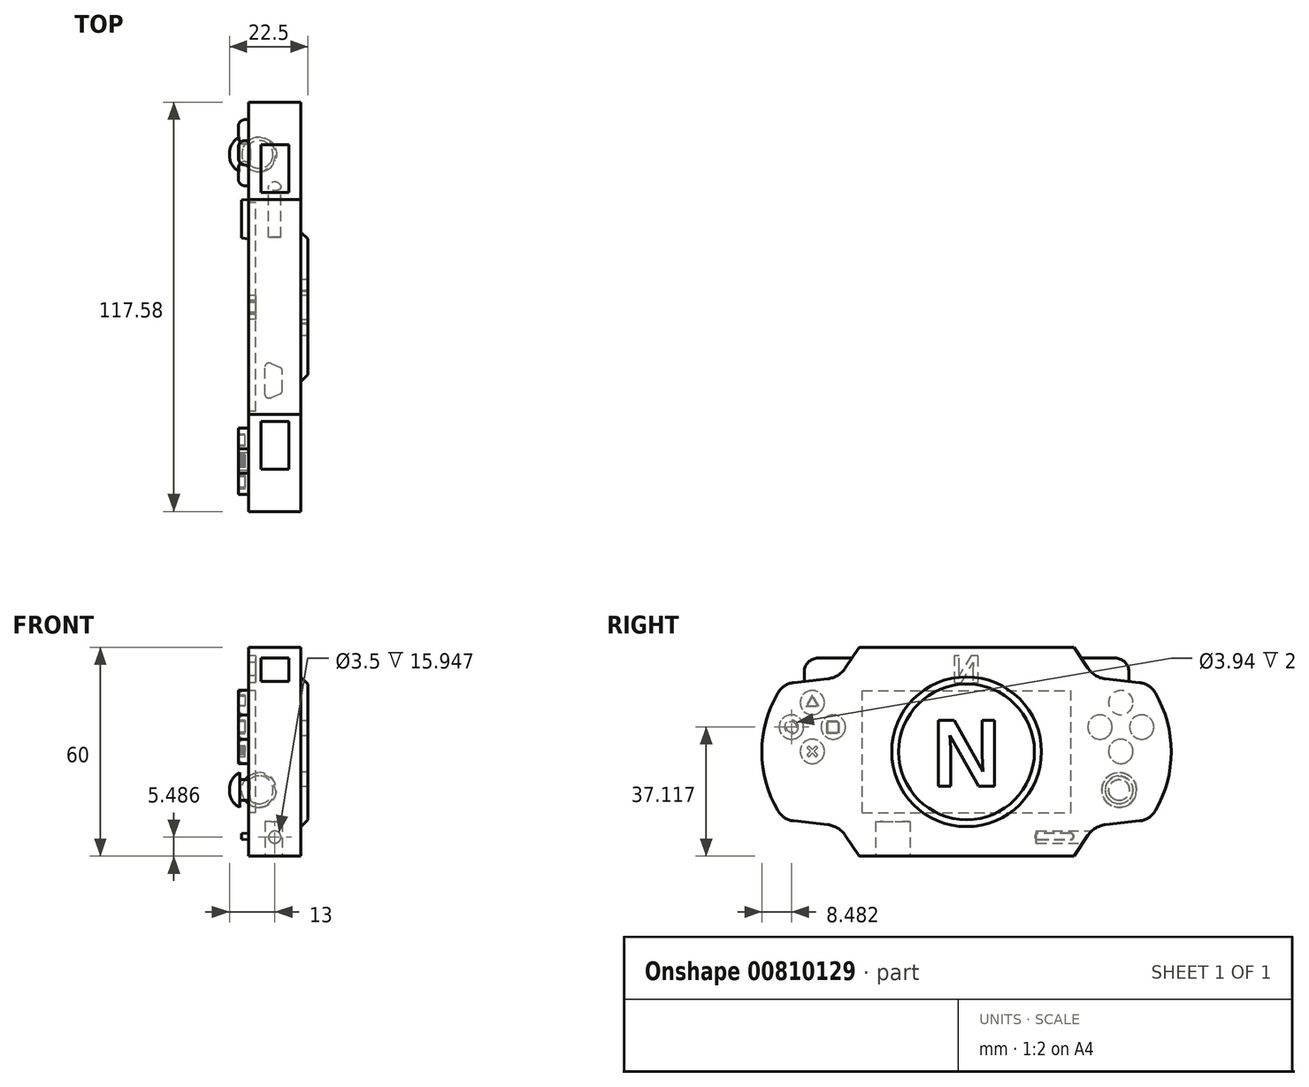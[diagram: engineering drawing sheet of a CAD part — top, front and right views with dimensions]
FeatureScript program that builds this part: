
annotation { "Feature Type Name" : "Feature", "Feature Type Description" : "" }
export const myFeature = defineFeature(function(context is Context, id is Id, definition is map)
    precondition{}
    {
        {
            var Q0;
            Q0=qCreatedBy(makeId("Right.planeOp"),FACE);
            var sketch = newSketch(context, id + "F0", { "sketchPlane" : qUnion([Q0])});
            skLineSegment(sketch, "E0.bottom", {"start": v(-30.9, -30) * mm, "end": v(30.9, -30) * mm});
            skLineSegment(sketch, "E0.top", {"start": v(-30.9, 30) * mm, "end": v(30.9, 30) * mm});
            skLineSegment(sketch, "E0.left", {"start": v(-52.5, -19.53) * mm, "end": v(-52.5, 19.53) * mm});
            skLineSegment(sketch, "E0.right", {"start": v(52.5, -19.53) * mm, "end": v(52.5, 19.53) * mm});
            skPoint(sketch, "E0.middle", {"position": v(0, 0) * mm});
            skLineSegment(sketch, "E1", {"start": v(49.7, 19.85) * mm, "end": v(46.21, 20.24) * mm});
            skLineSegment(sketch, "E2", {"start": v(34.87, 24.03) * mm, "end": v(30.9, 30) * mm});
            skPoint(sketch, "E3.visualSharp", {"position": v(36.68, 21.3) * mm});
            skArc(sketch, "E3.filletArc", {"start": v(34.87, 24.03) * mm, "mid": v(37.06, 21.92) * mm, "end": v(39.92, 20.94) * mm});
            skLineSegment(sketch, "E4", {"start": v(0, 39.51) * mm, "end": v(0, -39.4) * mm});
            skLineSegment(sketch, "E5.MirrorCS", {"start": v(-34.87, 24.03) * mm, "end": v(-30.9, 30) * mm});
            skPoint(sketch, "E6.MirrorP", {"position": v(-36.68, 21.3) * mm});
            skLineSegment(sketch, "E7.MirrorCS", {"start": v(-49.7, 19.85) * mm, "end": v(-46.21, 20.24) * mm});
            skArc(sketch, "E8.MirrorCS", {"start": v(-34.87, 24.03) * mm, "mid": v(-37.06, 21.92) * mm, "end": v(-39.92, 20.94) * mm});
            skLineSegment(sketch, "E9", {"start": v(46.21, 20.24) * mm, "end": v(39.92, 20.94) * mm});
            skLineSegment(sketch, "E10", {"start": v(59.6, 0) * mm, "end": v(-64.27, 0) * mm});
            skLineSegment(sketch, "E11.MirrorCS", {"start": v(49.7, -19.85) * mm, "end": v(46.21, -20.24) * mm});
            skLineSegment(sketch, "E12.MirrorCS", {"start": v(46.21, -20.24) * mm, "end": v(39.92, -20.94) * mm});
            skPoint(sketch, "E13.MirrorP", {"position": v(36.68, -21.3) * mm});
            skLineSegment(sketch, "E14.MirrorCS", {"start": v(34.87, -24.03) * mm, "end": v(30.9, -30) * mm});
            skArc(sketch, "E15.MirrorCS", {"start": v(34.87, -24.03) * mm, "mid": v(37.06, -21.92) * mm, "end": v(39.92, -20.94) * mm});
            skLineSegment(sketch, "E16.MirrorCS", {"start": v(-34.87, -24.03) * mm, "end": v(-30.9, -30) * mm});
            skArc(sketch, "E17.MirrorCS", {"start": v(-34.87, -24.03) * mm, "mid": v(-37.06, -21.92) * mm, "end": v(-39.92, -20.94) * mm});
            skLineSegment(sketch, "E18.MirrorCS", {"start": v(-49.7, -19.85) * mm, "end": v(-46.21, -20.24) * mm});
            skLineSegment(sketch, "E19", {"start": v(-46.21, 20.24) * mm, "end": v(-39.92, 20.94) * mm});
            skLineSegment(sketch, "E20", {"start": v(-46.21, -20.24) * mm, "end": v(-39.92, -20.94) * mm});
            skArc(sketch, "E21", {"start": v(54.2, -16.92) * mm, "mid": v(58.79, 0) * mm, "end": v(54.2, 16.92) * mm});
            skArc(sketch, "E22.MirrorCS", {"start": v(-54.2, -16.92) * mm, "mid": v(-58.79, 0) * mm, "end": v(-54.2, 16.92) * mm});
            skPoint(sketch, "E23.visualSharp", {"position": v(52.5, 19.53) * mm});
            skArc(sketch, "E23.filletArc", {"start": v(54.2, 16.92) * mm, "mid": v(52.3, 18.92) * mm, "end": v(49.7, 19.85) * mm});
            skPoint(sketch, "E24.visualSharp", {"position": v(52.5, -19.53) * mm});
            skArc(sketch, "E24.filletArc", {"start": v(49.7, -19.85) * mm, "mid": v(52.3, -18.92) * mm, "end": v(54.2, -16.92) * mm});
            skPoint(sketch, "E25.visualSharp", {"position": v(-52.5, 19.53) * mm});
            skArc(sketch, "E25.filletArc", {"start": v(-49.7, 19.85) * mm, "mid": v(-52.3, 18.92) * mm, "end": v(-54.2, 16.92) * mm});
            skPoint(sketch, "E26.visualSharp", {"position": v(-52.5, -19.53) * mm});
            skArc(sketch, "E26.filletArc", {"start": v(-54.2, -16.92) * mm, "mid": v(-52.3, -18.92) * mm, "end": v(-49.7, -19.85) * mm});
            skPoint(sketch, "E27.orphan", {"position": v(52.5, 30) * mm});
            skPoint(sketch, "E28.orphan", {"position": v(52.5, -30) * mm});
            skPoint(sketch, "E29.orphan", {"position": v(-52.5, -30) * mm});
            skPoint(sketch, "E30.orphan", {"position": v(-52.5, 30) * mm});
            skSolve(sketch);
        }
        {
            var Q0;
            Q0=qSketchRegion(id+"F0",true);
            extrude(context, id + "F1", {"entities" : qUnion([Q0]), "endBound" : BoundingType.SYMMETRIC, "depth" : 15 * mm, "offsetDistance" : 25 * mm});
        }
        {
            var Q0;
            Q0=qCreatedBy(makeId("Right.planeOp"),FACE);
            var sketch = newSketch(context, id + "F2", { "sketchPlane" : qUnion([Q0])});
            skLineSegment(sketch, "E31.bottom", {"start": v(29.71, 18.85) * mm, "end": v(46.63, 18.85) * mm});
            skLineSegment(sketch, "E31.top", {"start": v(29.71, 26.92) * mm, "end": v(42.63, 26.92) * mm});
            skLineSegment(sketch, "E31.left", {"start": v(29.71, 18.85) * mm, "end": v(29.71, 26.92) * mm});
            skLineSegment(sketch, "E31.right", {"start": v(46.63, 18.85) * mm, "end": v(46.63, 22.92) * mm});
            skPoint(sketch, "E31.middle", {"position": v(38.17, 22.88) * mm});
            skLineSegment(sketch, "E32", {"start": v(0, 47.3) * mm, "end": v(0, -44.62) * mm});
            skLineSegment(sketch, "E33.MirrorCS", {"start": v(-29.71, 26.92) * mm, "end": v(-42.63, 26.92) * mm});
            skLineSegment(sketch, "E34.MirrorCS", {"start": v(-46.63, 18.85) * mm, "end": v(-46.63, 22.92) * mm});
            skLineSegment(sketch, "E35.MirrorCS", {"start": v(-29.71, 18.85) * mm, "end": v(-29.71, 26.92) * mm});
            skLineSegment(sketch, "E36.MirrorCS", {"start": v(-29.71, 18.85) * mm, "end": v(-46.63, 18.85) * mm});
            skPoint(sketch, "E37.visualSharp", {"position": v(46.63, 26.92) * mm});
            skArc(sketch, "E37.filletArc", {"start": v(46.63, 22.92) * mm, "mid": v(45.46, 25.75) * mm, "end": v(42.63, 26.92) * mm});
            skPoint(sketch, "E38.visualSharp", {"position": v(-46.63, 26.92) * mm});
            skArc(sketch, "E38.filletArc", {"start": v(-42.63, 26.92) * mm, "mid": v(-45.46, 25.75) * mm, "end": v(-46.63, 22.92) * mm});
            skSolve(sketch);
        }
        {
            var Q0;
            Q0=makeQuery(id+"F2.imprint","IMPRINT",FACE,{"disambiguationData":[TD([[makeQuery(id+"F2.imprint","IMPRINT",EDGE,{"derivedFrom":sQuery(id+"F2.wireOp",EDGE,"E31.bottom")}),1.0]])]});
            var Q1;
            Q1=makeQuery(id+"F2.imprint","IMPRINT",FACE,{"disambiguationData":[TD([[makeQuery(id+"F2.imprint","IMPRINT",EDGE,{"derivedFrom":sQuery(id+"F2.wireOp",EDGE,"E33.MirrorCS")}),1.0]])]});
            var Q2;
            Q2=qConstructionFilter(qBodyType(qCreatedBy(id+"F2",EDGE),BodyType.WIRE),ConstructionObject.NO);
            extrude(context, id + "F3", {"entities" : qUnion([Q0, Q1]), "operationType" : NewBodyOperationType.ADD, "surfaceEntities" : qUnion([Q2]), "endBound" : BoundingType.SYMMETRIC, "depth" : 8 * mm, "offsetDistance" : 25 * mm});
        }
        {
            var Q0;
            Q0=makeQuery(id+"F1.opExtrude","CAP_FACE",FACE,{"disambiguationData":[OSD([sQuery(id+"F0.wireOp",EDGE,"E0.bottom"),sQuery(id+"F0.wireOp",EDGE,"E0.top"),sQuery(id+"F0.wireOp",EDGE,"E1"),sQuery(id+"F0.wireOp",EDGE,"E2"),sQuery(id+"F0.wireOp",EDGE,"E3.filletArc"),sQuery(id+"F0.wireOp",EDGE,"E5.MirrorCS"),sQuery(id+"F0.wireOp",EDGE,"E7.MirrorCS"),sQuery(id+"F0.wireOp",EDGE,"E8.MirrorCS"),sQuery(id+"F0.wireOp",EDGE,"E9"),sQuery(id+"F0.wireOp",EDGE,"E11.MirrorCS"),sQuery(id+"F0.wireOp",EDGE,"E12.MirrorCS"),sQuery(id+"F0.wireOp",EDGE,"E14.MirrorCS"),sQuery(id+"F0.wireOp",EDGE,"E15.MirrorCS"),sQuery(id+"F0.wireOp",EDGE,"E16.MirrorCS"),sQuery(id+"F0.wireOp",EDGE,"E17.MirrorCS"),sQuery(id+"F0.wireOp",EDGE,"E18.MirrorCS"),sQuery(id+"F0.wireOp",EDGE,"E19"),sQuery(id+"F0.wireOp",EDGE,"E20"),sQuery(id+"F0.wireOp",EDGE,"E21"),sQuery(id+"F0.wireOp",EDGE,"E22.MirrorCS"),sQuery(id+"F0.wireOp",EDGE,"E23.filletArc"),sQuery(id+"F0.wireOp",EDGE,"E24.filletArc"),sQuery(id+"F0.wireOp",EDGE,"E25.filletArc"),sQuery(id+"F0.wireOp",EDGE,"E26.filletArc")])],"isStart":true});
            var sketch = newSketch(context, id + "F4", { "sketchPlane" : qUnion([Q0])});
            skLineSegment(sketch, "E39.bottom", {"start": v(30, -17.5) * mm, "end": v(-30, -17.5) * mm});
            skLineSegment(sketch, "E39.top", {"start": v(30, 17.5) * mm, "end": v(-30, 17.5) * mm});
            skLineSegment(sketch, "E39.left", {"start": v(30, -17.5) * mm, "end": v(30, 17.5) * mm});
            skLineSegment(sketch, "E39.right", {"start": v(-30, -17.5) * mm, "end": v(-30, 17.5) * mm});
            skPoint(sketch, "E39.middle", {"position": v(0, 0) * mm});
            skSolve(sketch);
        }
        {
            var Q0;
            Q0=makeQuery(id+"F4.imprint","IMPRINT",FACE,{"disambiguationData":[TD([[makeQuery(id+"F4.imprint","IMPRINT",EDGE,{"derivedFrom":sQuery(id+"F4.wireOp",EDGE,"E39.bottom")}),-1.0]])]});
            extrude(context, id + "F5", {"entities" : qUnion([Q0]), "operationType" : NewBodyOperationType.REMOVE, "oppositeDirection" : true, "depth" : 2 * mm, "offsetDistance" : 25 * mm});
        }
        {
            var Q0;
            Q0=makeQuery(id+"F1.opExtrude","CAP_FACE",FACE,{"disambiguationData":[OSD([sQuery(id+"F0.wireOp",EDGE,"E0.bottom"),sQuery(id+"F0.wireOp",EDGE,"E0.top"),sQuery(id+"F0.wireOp",EDGE,"E1"),sQuery(id+"F0.wireOp",EDGE,"E2"),sQuery(id+"F0.wireOp",EDGE,"E3.filletArc"),sQuery(id+"F0.wireOp",EDGE,"E5.MirrorCS"),sQuery(id+"F0.wireOp",EDGE,"E7.MirrorCS"),sQuery(id+"F0.wireOp",EDGE,"E8.MirrorCS"),sQuery(id+"F0.wireOp",EDGE,"E9"),sQuery(id+"F0.wireOp",EDGE,"E11.MirrorCS"),sQuery(id+"F0.wireOp",EDGE,"E12.MirrorCS"),sQuery(id+"F0.wireOp",EDGE,"E14.MirrorCS"),sQuery(id+"F0.wireOp",EDGE,"E15.MirrorCS"),sQuery(id+"F0.wireOp",EDGE,"E16.MirrorCS"),sQuery(id+"F0.wireOp",EDGE,"E17.MirrorCS"),sQuery(id+"F0.wireOp",EDGE,"E18.MirrorCS"),sQuery(id+"F0.wireOp",EDGE,"E19"),sQuery(id+"F0.wireOp",EDGE,"E20"),sQuery(id+"F0.wireOp",EDGE,"E21"),sQuery(id+"F0.wireOp",EDGE,"E22.MirrorCS"),sQuery(id+"F0.wireOp",EDGE,"E23.filletArc"),sQuery(id+"F0.wireOp",EDGE,"E24.filletArc"),sQuery(id+"F0.wireOp",EDGE,"E25.filletArc"),sQuery(id+"F0.wireOp",EDGE,"E26.filletArc")])],"isStart":true});
            var sketch = newSketch(context, id + "F6", { "sketchPlane" : qUnion([Q0])});
            skLineSegment(sketch, "E40", {"start": v(-50.3, 7.12) * mm, "end": v(-44.3, 7.12) * mm});
            skLineSegment(sketch, "E41", {"start": v(-44.3, 7.12) * mm, "end": v(-38.3, 7.12) * mm});
            skLineSegment(sketch, "E42", {"start": v(-44.3, 7.12) * mm, "end": v(-44.3, 0.12) * mm});
            skLineSegment(sketch, "E43", {"start": v(-44.3, 7.12) * mm, "end": v(-44.3, 14.12) * mm});
            skCircle(sketch, "E44", {"center": v(-44.3, 14.12) * mm, "radius": 3.5 * mm});
            skCircle(sketch, "E45", {"center": v(-50.3, 7.12) * mm, "radius": 3.5 * mm});
            skCircle(sketch, "E46", {"center": v(-38.3, 7.12) * mm, "radius": 3.5 * mm});
            skCircle(sketch, "E47", {"center": v(-44.3, 0.12) * mm, "radius": 3.5 * mm});
            skLineSegment(sketch, "E48", {"start": v(0, 48.36) * mm, "end": v(0, -44.18) * mm});
            skPoint(sketch, "E48.endSnap0", {"position": v(0, -30) * mm});
            skCircle(sketch, "E49.MirrorC", {"center": v(44.3, 14.12) * mm, "radius": 3.5 * mm});
            skCircle(sketch, "E50.MirrorC", {"center": v(38.3, 7.12) * mm, "radius": 3.5 * mm});
            skCircle(sketch, "E51.MirrorC", {"center": v(44.3, 0.12) * mm, "radius": 3.5 * mm});
            skCircle(sketch, "E52.MirrorC", {"center": v(50.3, 7.12) * mm, "radius": 3.5 * mm});
            skSolve(sketch);
        }
        {
            var Q0;
            Q0 = qSketchRegion(id + "F6", true);
            extrude(context, id + "F7", {"entities" : qUnion([Q0]), "operationType" : NewBodyOperationType.ADD, "depth" : 3 * mm, "offsetDistance" : 25 * mm});
        }
        {
            var Q0;
            Q0=makeQuery(id+"F7.opExtrude","CAP_FACE",FACE,{"disambiguationData":[OSD([sQuery(id+"F6.wireOp",EDGE,"E44")])],"isStart":false});
            var Q1;
            Q1=makeQuery(id+"F7.opExtrude","CAP_FACE",FACE,{"disambiguationData":[OSD([sQuery(id+"F6.wireOp",EDGE,"E46")])],"isStart":false});
            var Q2;
            Q2=makeQuery(id+"F7.opExtrude","CAP_FACE",FACE,{"disambiguationData":[OSD([sQuery(id+"F6.wireOp",EDGE,"E47")])],"isStart":false});
            var Q3;
            Q3=makeQuery(id+"F7.opExtrude","CAP_FACE",FACE,{"disambiguationData":[OSD([sQuery(id+"F6.wireOp",EDGE,"E45")])],"isStart":false});
            fillet(context, id + "F8", {"entities" : qUnion([Q0, Q1, Q2, Q3]), "radius" : 2 * mm, "tangentPropagation" : true, "allowEdgeOverflow" : false});
        }
        {
            var Q0;
            Q0=makeQuery(id+"F1.opExtrude","CAP_FACE",FACE,{"disambiguationData":[OSD([sQuery(id+"F0.wireOp",EDGE,"E0.bottom"),sQuery(id+"F0.wireOp",EDGE,"E0.top"),sQuery(id+"F0.wireOp",EDGE,"E1"),sQuery(id+"F0.wireOp",EDGE,"E2"),sQuery(id+"F0.wireOp",EDGE,"E3.filletArc"),sQuery(id+"F0.wireOp",EDGE,"E5.MirrorCS"),sQuery(id+"F0.wireOp",EDGE,"E7.MirrorCS"),sQuery(id+"F0.wireOp",EDGE,"E8.MirrorCS"),sQuery(id+"F0.wireOp",EDGE,"E9"),sQuery(id+"F0.wireOp",EDGE,"E11.MirrorCS"),sQuery(id+"F0.wireOp",EDGE,"E12.MirrorCS"),sQuery(id+"F0.wireOp",EDGE,"E14.MirrorCS"),sQuery(id+"F0.wireOp",EDGE,"E15.MirrorCS"),sQuery(id+"F0.wireOp",EDGE,"E16.MirrorCS"),sQuery(id+"F0.wireOp",EDGE,"E17.MirrorCS"),sQuery(id+"F0.wireOp",EDGE,"E18.MirrorCS"),sQuery(id+"F0.wireOp",EDGE,"E19"),sQuery(id+"F0.wireOp",EDGE,"E20"),sQuery(id+"F0.wireOp",EDGE,"E21"),sQuery(id+"F0.wireOp",EDGE,"E22.MirrorCS"),sQuery(id+"F0.wireOp",EDGE,"E23.filletArc"),sQuery(id+"F0.wireOp",EDGE,"E24.filletArc"),sQuery(id+"F0.wireOp",EDGE,"E25.filletArc"),sQuery(id+"F0.wireOp",EDGE,"E26.filletArc")])],"isStart":false});
            var sketch = newSketch(context, id + "F9", { "sketchPlane" : qUnion([Q0])});
            skCircle(sketch, "E53", {"center": v(0, 0) * mm, "radius": 22.5 * mm});
            skSolve(sketch);
        }
        {
            var Q0;
            Q0 = qSketchRegion(id + "F9", true);
            extrude(context, id + "F10", {"entities" : qUnion([Q0]), "operationType" : NewBodyOperationType.ADD, "depth" : 2 * mm, "offsetDistance" : 25 * mm});
        }
        {
            var Q0;
            Q0=makeQuery(id+"F10.opExtrude","CAP_EDGE",EDGE,{"disambiguationData":[OSD([sQuery(id+"F9.wireOp",EDGE,"E53")])],"isStart":false});
            chamfer(context, id + "F11", {"entities" : qUnion([Q0]), "width" : 3 * mm, "tangentPropagation" : true});
        }
        {
            var Q0;
            Q0=makeQuery(id+"F10.opExtrude","CAP_FACE",FACE,{"disambiguationData":[OSD([sQuery(id+"F9.wireOp",EDGE,"E53")])],"isStart":false});
            var sketch = newSketch(context, id + "F12", { "sketchPlane" : qUnion([Q0])});
            skText(sketch, "E54", { "text": "N\n", "fontName": "Arimo-Bold.ttf"});
            skPoint(sketch, "E55", {"position": v(0, 0) * mm});
            const initialGuessF12  = {"E54": [-0.00995, -0.00989, 1, 0, 0.01978]};
            skSetInitialGuess(sketch, initialGuessF12);
            skSolve(sketch);
        }
        {
            var Q0;
            Q0 = qSketchRegion(id + "F12", true);
            extrude(context, id + "F13", {"entities" : qUnion([Q0]), "operationType" : NewBodyOperationType.REMOVE, "oppositeDirection" : true, "depth" : 2 * mm, "offsetDistance" : 25 * mm});
        }
        {
            var Q0;
            Q0=makeQuery(id+"F1.opExtrude","CAP_FACE",FACE,{"disambiguationData":[OSD([sQuery(id+"F0.wireOp",EDGE,"E0.bottom"),sQuery(id+"F0.wireOp",EDGE,"E0.top"),sQuery(id+"F0.wireOp",EDGE,"E1"),sQuery(id+"F0.wireOp",EDGE,"E2"),sQuery(id+"F0.wireOp",EDGE,"E3.filletArc"),sQuery(id+"F0.wireOp",EDGE,"E5.MirrorCS"),sQuery(id+"F0.wireOp",EDGE,"E7.MirrorCS"),sQuery(id+"F0.wireOp",EDGE,"E8.MirrorCS"),sQuery(id+"F0.wireOp",EDGE,"E9"),sQuery(id+"F0.wireOp",EDGE,"E11.MirrorCS"),sQuery(id+"F0.wireOp",EDGE,"E12.MirrorCS"),sQuery(id+"F0.wireOp",EDGE,"E14.MirrorCS"),sQuery(id+"F0.wireOp",EDGE,"E15.MirrorCS"),sQuery(id+"F0.wireOp",EDGE,"E16.MirrorCS"),sQuery(id+"F0.wireOp",EDGE,"E17.MirrorCS"),sQuery(id+"F0.wireOp",EDGE,"E18.MirrorCS"),sQuery(id+"F0.wireOp",EDGE,"E19"),sQuery(id+"F0.wireOp",EDGE,"E20"),sQuery(id+"F0.wireOp",EDGE,"E21"),sQuery(id+"F0.wireOp",EDGE,"E22.MirrorCS"),sQuery(id+"F0.wireOp",EDGE,"E23.filletArc"),sQuery(id+"F0.wireOp",EDGE,"E24.filletArc"),sQuery(id+"F0.wireOp",EDGE,"E25.filletArc"),sQuery(id+"F0.wireOp",EDGE,"E26.filletArc")])],"isStart":true});
            var sketch = newSketch(context, id + "F14", { "sketchPlane" : qUnion([Q0])});
            skLineSegment(sketch, "E56.bottom", {"start": v(-20.58, -25.31) * mm, "end": v(-29.84, -25.31) * mm});
            skLineSegment(sketch, "E56.top", {"start": v(-20.58, -23.31) * mm, "end": v(-29.84, -23.31) * mm});
            skPoint(sketch, "E56.middle", {"position": v(-25.21, -24.31) * mm});
            skLineSegment(sketch, "E57", {"start": v(-30.84, -24.31) * mm, "end": v(-30.84, -24.31) * mm});
            skLineSegment(sketch, "E58.MirrorCS", {"start": v(-19.58, -24.31) * mm, "end": v(-19.58, -24.31) * mm});
            skPoint(sketch, "E59.end.orphan", {"position": v(-25.21, -27.04) * mm});
            skPoint(sketch, "E60.visualSharp", {"position": v(-30.21, -23.31) * mm});
            skArc(sketch, "E60.filletArc", {"start": v(-29.84, -23.31) * mm, "mid": v(-30.55, -23.6) * mm, "end": v(-30.84, -24.31) * mm});
            skPoint(sketch, "E61.visualSharp", {"position": v(-30.21, -25.31) * mm});
            skArc(sketch, "E61.filletArc", {"start": v(-30.84, -24.31) * mm, "mid": v(-30.55, -25.02) * mm, "end": v(-29.84, -25.31) * mm});
            skPoint(sketch, "E62.visualSharp", {"position": v(-20.21, -23.31) * mm});
            skArc(sketch, "E62.filletArc", {"start": v(-19.58, -24.31) * mm, "mid": v(-19.87, -23.6) * mm, "end": v(-20.58, -23.31) * mm});
            skPoint(sketch, "E63.visualSharp", {"position": v(-20.21, -25.31) * mm});
            skArc(sketch, "E63.filletArc", {"start": v(-20.58, -25.31) * mm, "mid": v(-19.87, -25.02) * mm, "end": v(-19.58, -24.31) * mm});
            skSolve(sketch);
        }
        {
            var Q0;
            Q0 = qSketchRegion(id + "F14", true);
            extrude(context, id + "F15", {"entities" : qUnion([Q0]), "operationType" : NewBodyOperationType.ADD, "depth" : 2 * mm, "offsetDistance" : 25 * mm, "hasDraft" : true, "draftAngle" : 5 * degree, "draftPullDirection" : true});
        }
        {
            var Q0;
            Q0=makeQuery(id+"F1.opExtrude","CAP_FACE",FACE,{"disambiguationData":[OSD([sQuery(id+"F0.wireOp",EDGE,"E0.bottom"),sQuery(id+"F0.wireOp",EDGE,"E0.top"),sQuery(id+"F0.wireOp",EDGE,"E1"),sQuery(id+"F0.wireOp",EDGE,"E2"),sQuery(id+"F0.wireOp",EDGE,"E3.filletArc"),sQuery(id+"F0.wireOp",EDGE,"E5.MirrorCS"),sQuery(id+"F0.wireOp",EDGE,"E7.MirrorCS"),sQuery(id+"F0.wireOp",EDGE,"E8.MirrorCS"),sQuery(id+"F0.wireOp",EDGE,"E9"),sQuery(id+"F0.wireOp",EDGE,"E11.MirrorCS"),sQuery(id+"F0.wireOp",EDGE,"E12.MirrorCS"),sQuery(id+"F0.wireOp",EDGE,"E14.MirrorCS"),sQuery(id+"F0.wireOp",EDGE,"E15.MirrorCS"),sQuery(id+"F0.wireOp",EDGE,"E16.MirrorCS"),sQuery(id+"F0.wireOp",EDGE,"E17.MirrorCS"),sQuery(id+"F0.wireOp",EDGE,"E18.MirrorCS"),sQuery(id+"F0.wireOp",EDGE,"E19"),sQuery(id+"F0.wireOp",EDGE,"E20"),sQuery(id+"F0.wireOp",EDGE,"E21"),sQuery(id+"F0.wireOp",EDGE,"E22.MirrorCS"),sQuery(id+"F0.wireOp",EDGE,"E23.filletArc"),sQuery(id+"F0.wireOp",EDGE,"E24.filletArc"),sQuery(id+"F0.wireOp",EDGE,"E25.filletArc"),sQuery(id+"F0.wireOp",EDGE,"E26.filletArc")])],"isStart":true});
            var sketch = newSketch(context, id + "F16", { "sketchPlane" : qUnion([Q0])});
            skText(sketch, "E64", { "text": "N", "fontName": "OpenSans-Bold.ttf"});
            const initialGuessF16  = {"E64": [-0.00427, 0.01987, 1, 0, 0.0078]};
            skSetInitialGuess(sketch, initialGuessF16);
            skSolve(sketch);
        }
        {
            var Q0;
            Q0 = qSketchRegion(id + "F16", true);
            extrude(context, id + "F17", {"entities" : qUnion([Q0]), "operationType" : NewBodyOperationType.REMOVE, "oppositeDirection" : true, "depth" : 2 * mm, "offsetDistance" : 25 * mm});
        }
        {
            var Q0;
            Q0=qCreatedBy(makeId("Right.planeOp"),FACE);
            cPlane(context, id + "F18", {"entities" : qUnion([Q0]), "cplaneType" : CPlaneType.OFFSET, "offset" : 4.5 * mm, "oppositeDirection" : true, "width" : 150 * mm, "height" : 150 * mm});
        }
        {
            var Q0;
            Q0=qCreatedBy(id+"F18.planeOp",FACE);
            var sketch = newSketch(context, id + "F19", { "sketchPlane" : qUnion([Q0])});
            skCircle(sketch, "E65", {"center": v(43.82, -10.98) * mm, "radius": 5 * mm});
            skLineSegment(sketch, "E66", {"start": v(43.82, -5.98) * mm, "end": v(43.82, -15.98) * mm});
            skSolve(sketch);
        }
        {
            var Q0;
            {var subQ0=sQuery(id+"F19.wireOp",EDGE,"E66");Q0=makeQuery(id+"F19.imprint","IMPRINT",FACE,{"disambiguationData":[TD([[makeQuery(id+"F19.imprint","IMPRINT",EDGE,{"derivedFrom":subQ0}),1.0]])]});}
            var Q1;
            Q1=sQuery(id+"F19.wireOp",EDGE,"E66");
            revolve(context, id + "F20", {"operationType" : NewBodyOperationType.REMOVE, "surfaceOperationType" : NewSurfaceOperationType.NEW, "entities" : qUnion([Q0]), "axis" : qUnion([Q1]), "revolveType" : RevolveType.FULL});
        }
        {
            var Q0;
            Q0=qCreatedBy(makeId("Right.planeOp"),FACE);
            cPlane(context, id + "F21", {"entities" : qUnion([Q0]), "cplaneType" : CPlaneType.OFFSET, "offset" : 4.5 * mm, "oppositeDirection" : true, "width" : 150 * mm, "height" : 150 * mm});
        }
        {
            var Q0;
            Q0=qCreatedBy(id+"F21.planeOp",FACE);
            var sketch = newSketch(context, id + "F22", { "sketchPlane" : qUnion([Q0])});
            skCircle(sketch, "E67", {"center": v(43.82, -10.92) * mm, "radius": 4 * mm});
            skLineSegment(sketch, "E68", {"start": v(43.82, -4.76) * mm, "end": v(43.82, -17.6) * mm});
            skSolve(sketch);
        }
        {
            var Q0;
            {var subQ0=sQuery(id+"F22.wireOp",EDGE,"E68");var subQ1=sQuery(id+"F22.wireOp",EDGE,"E67");var subQ2=makeQuery(id+"F22.imprint","INTERSECT",VERTEX,{"disambiguationData":[OD(0.0)],"derivedFrom":[subQ1,subQ0]});Q0=makeQuery(id+"F22.imprint","IMPRINT",FACE,{"disambiguationData":[TD([[makeQuery(id+"F22.imprint","IMPRINT",EDGE,{"disambiguationData":[TD([[subQ2,1.0]])],"derivedFrom":subQ1}),1.0]])]});}
            var Q1;
            Q1=sQuery(id+"F22.wireOp",EDGE,"E68");
            revolve(context, id + "F23", {"surfaceOperationType" : NewSurfaceOperationType.NEW, "entities" : qUnion([Q0]), "axis" : qUnion([Q1]), "revolveType" : RevolveType.FULL});
        }
        {
            var Q0;
            Q0=qCreatedBy(makeId("Right.planeOp"),FACE);
            cPlane(context, id + "F24", {"entities" : qUnion([Q0]), "cplaneType" : CPlaneType.OFFSET, "offset" : 7 * mm, "oppositeDirection" : true, "width" : 150 * mm, "height" : 150 * mm});
        }
        {
            var Q0;
            Q0=qCreatedBy(id+"F24.planeOp",FACE);
            var sketch = newSketch(context, id + "F25", { "sketchPlane" : qUnion([Q0])});
            skCircle(sketch, "E69", {"center": v(43.82, -11) * mm, "radius": 3 * mm});
            skSolve(sketch);
        }
        {
            var Q0;
            Q0 = qSketchRegion(id + "F25", true);
            extrude(context, id + "F26", {"entities" : qUnion([Q0]), "operationType" : NewBodyOperationType.ADD, "oppositeDirection" : true, "depth" : 3 * mm, "offsetDistance" : 25 * mm});
        }
        {
            var Q0;
            Q0=makeQuery(id+"F26.opExtrude","CAP_FACE",FACE,{"disambiguationData":[OSD([sQuery(id+"F25.wireOp",EDGE,"E69")])],"isStart":false});
            var sketch = newSketch(context, id + "F27", { "sketchPlane" : qUnion([Q0])});
            skCircle(sketch, "E70", {"center": v(-43.82, -11) * mm, "radius": 5 * mm});
            skSolve(sketch);
        }
        {
            var Q0;
            Q0 = qSketchRegion(id + "F27", true);
            extrude(context, id + "F28", {"entities" : qUnion([Q0]), "operationType" : NewBodyOperationType.ADD, "depth" : 3 * mm, "offsetDistance" : 25 * mm});
        }
        {
            var Q0;
            Q0=makeQuery(id+"F28.opExtrude","CAP_EDGE",EDGE,{"disambiguationData":[OSD([sQuery(id+"F27.wireOp",EDGE,"E70")])],"isStart":false});
            fillet(context, id + "F29", {"entities" : qUnion([Q0]), "radius" : 5 * mm, "tangentPropagation" : true, "allowEdgeOverflow" : false});
        }
        {
            var Q0;
            Q0=makeQuery(id+"F7.opExtrude","CAP_FACE",FACE,{"disambiguationData":[OSD([sQuery(id+"F6.wireOp",EDGE,"E50.MirrorC")])],"isStart":false});
            var sketch = newSketch(context, id + "F30", { "sketchPlane" : qUnion([Q0])});
            skLineSegment(sketch, "E71.bottom", {"start": v(40.06, 5.37) * mm, "end": v(36.56, 5.37) * mm});
            skLineSegment(sketch, "E71.top", {"start": v(40.06, 8.87) * mm, "end": v(36.56, 8.87) * mm});
            skLineSegment(sketch, "E71.left", {"start": v(40.06, 5.37) * mm, "end": v(40.06, 8.87) * mm});
            skLineSegment(sketch, "E71.right", {"start": v(36.56, 5.37) * mm, "end": v(36.56, 8.87) * mm});
            skPoint(sketch, "E71.middle", {"position": v(38.3, 7.12) * mm});
            skLineSegment(sketch, "E72.bottom", {"start": v(39.8, 5.62) * mm, "end": v(36.8, 5.62) * mm});
            skLineSegment(sketch, "E72.top", {"start": v(39.8, 8.62) * mm, "end": v(36.8, 8.62) * mm});
            skLineSegment(sketch, "E72.left", {"start": v(39.8, 5.62) * mm, "end": v(39.8, 8.62) * mm});
            skLineSegment(sketch, "E72.right", {"start": v(36.8, 5.62) * mm, "end": v(36.8, 8.62) * mm});
            skSolve(sketch);
        }
        {
            var Q0;
            Q0 = qSketchRegion(id + "F30", true);
            extrude(context, id + "F31", {"entities" : qUnion([Q0]), "operationType" : NewBodyOperationType.REMOVE, "oppositeDirection" : true, "depth" : 2 * mm, "offsetDistance" : 25 * mm});
        }
        {
            var Q0;
            Q0=makeQuery(id+"F7.opExtrude","CAP_FACE",FACE,{"disambiguationData":[OSD([sQuery(id+"F6.wireOp",EDGE,"E52.MirrorC")])],"isStart":false});
            var sketch = newSketch(context, id + "F32", { "sketchPlane" : qUnion([Q0])});
            skCircle(sketch, "E73", {"center": v(50.3, 7.12) * mm, "radius": 1.97 * mm});
            skCircle(sketch, "E74", {"center": v(50.3, 7.12) * mm, "radius": 1.5 * mm});
            skSolve(sketch);
        }
        {
            var Q0;
            Q0=makeQuery(id+"F32.imprint","IMPRINT",FACE,{"disambiguationData":[TD([[makeQuery(id+"F32.imprint","IMPRINT",EDGE,{"derivedFrom":sQuery(id+"F32.wireOp",EDGE,"E73")}),1.0]])]});
            extrude(context, id + "F33", {"entities" : qUnion([Q0]), "operationType" : NewBodyOperationType.REMOVE, "oppositeDirection" : true, "depth" : 2 * mm, "offsetDistance" : 25 * mm});
        }
        {
            var Q0;
            Q0=makeQuery(id+"F7.opExtrude","CAP_FACE",FACE,{"disambiguationData":[OSD([sQuery(id+"F6.wireOp",EDGE,"E49.MirrorC")])],"isStart":false});
            var sketch = newSketch(context, id + "F34", { "sketchPlane" : qUnion([Q0])});
            skLineSegment(sketch, "E75.0", {"start": v(46.16, 13.05) * mm, "end": v(42.46, 13.05) * mm});
            skLineSegment(sketch, "E75.1", {"start": v(42.46, 13.05) * mm, "end": v(44.3, 16.25) * mm});
            skLineSegment(sketch, "E75.2", {"start": v(44.3, 16.25) * mm, "end": v(46.16, 13.05) * mm});
            skPoint(sketch, "E75.0.midPoint", {"position": v(44.3, 13.05) * mm});
            skPoint(sketch, "E75.cCircle.center.orphan", {"position": v(44.3, 14.12) * mm});
            skLineSegment(sketch, "E76.0", {"start": v(44.3, 15.79) * mm, "end": v(45.75, 13.28) * mm});
            skLineSegment(sketch, "E76.1", {"start": v(42.86, 13.28) * mm, "end": v(44.3, 15.79) * mm});
            skLineSegment(sketch, "E76.2", {"start": v(45.75, 13.28) * mm, "end": v(42.86, 13.28) * mm});
            skSolve(sketch);
        }
        {
            var Q0;
            Q0=makeQuery(id+"F34.imprint","IMPRINT",FACE,{"disambiguationData":[TD([[makeQuery(id+"F34.imprint","IMPRINT",EDGE,{"derivedFrom":sQuery(id+"F34.wireOp",EDGE,"E75.0")}),-1.0]])]});
            extrude(context, id + "F35", {"entities" : qUnion([Q0]), "operationType" : NewBodyOperationType.ADD, "oppositeDirection" : true, "depth" : 2 * mm, "offsetDistance" : 25 * mm});
        }
        {
            var Q0;
            Q0=makeQuery(id+"F7.opExtrude","CAP_FACE",FACE,{"disambiguationData":[OSD([sQuery(id+"F6.wireOp",EDGE,"E49.MirrorC")])],"isStart":false});
            var sketch = newSketch(context, id + "F36", { "sketchPlane" : qUnion([Q0])});
            skLineSegment(sketch, "E77.0", {"start": v(46.16, 13.05) * mm, "end": v(42.46, 13.05) * mm});
            skLineSegment(sketch, "E77.1", {"start": v(42.46, 13.05) * mm, "end": v(44.3, 16.25) * mm});
            skLineSegment(sketch, "E77.2", {"start": v(44.3, 16.25) * mm, "end": v(46.16, 13.05) * mm});
            skPoint(sketch, "E77.0.midPoint", {"position": v(44.3, 13.05) * mm});
            skPoint(sketch, "E77.cCircle.center.orphan", {"position": v(44.3, 14.12) * mm});
            skLineSegment(sketch, "E78.0", {"start": v(45.8, 13.25) * mm, "end": v(42.8, 13.25) * mm});
            skLineSegment(sketch, "E78.1", {"start": v(42.8, 13.25) * mm, "end": v(44.3, 15.85) * mm});
            skLineSegment(sketch, "E78.2", {"start": v(44.3, 15.85) * mm, "end": v(45.8, 13.25) * mm});
            skPoint(sketch, "E78.0.midPoint", {"position": v(44.3, 13.25) * mm});
            skSolve(sketch);
        }
        {
            var Q0;
            Q0 = qSketchRegion(id + "F36", true);
            extrude(context, id + "F37", {"entities" : qUnion([Q0]), "operationType" : NewBodyOperationType.REMOVE, "oppositeDirection" : true, "depth" : 2 * mm, "offsetDistance" : 25 * mm});
        }
        {
            var Q0;
            Q0=makeQuery(id+"F7.opExtrude","CAP_FACE",FACE,{"disambiguationData":[OSD([sQuery(id+"F6.wireOp",EDGE,"E51.MirrorC")])],"isStart":false});
            var sketch = newSketch(context, id + "F38", { "sketchPlane" : qUnion([Q0])});
            skLineSegment(sketch, "E79.bottom", {"start": v(45.88, -0.93) * mm, "end": v(45.35, -1.45) * mm});
            skLineSegment(sketch, "E79.top", {"start": v(43.26, 1.69) * mm, "end": v(42.74, 1.16) * mm});
            skLineSegment(sketch, "E79.left", {"start": v(45.88, 1.16) * mm, "end": v(45.35, 1.69) * mm});
            skLineSegment(sketch, "E79.right", {"start": v(43.26, -1.45) * mm, "end": v(42.74, -0.93) * mm});
            skPoint(sketch, "E79.middle", {"position": v(44.3, 0.12) * mm});
            skLineSegment(sketch, "E80.top", {"start": v(43.26, 1.69) * mm, "end": v(44.3, 0.64) * mm});
            skLineSegment(sketch, "E80.right", {"start": v(45.35, 1.69) * mm, "end": v(44.3, 0.64) * mm});
            skLineSegment(sketch, "E81.top", {"start": v(42.74, -0.93) * mm, "end": v(43.78, 0.12) * mm});
            skLineSegment(sketch, "E81.right", {"start": v(42.74, 1.16) * mm, "end": v(43.78, 0.12) * mm});
            skLineSegment(sketch, "E82.top", {"start": v(43.26, -1.45) * mm, "end": v(44.3, -0.4) * mm});
            skLineSegment(sketch, "E82.right", {"start": v(45.35, -1.45) * mm, "end": v(44.3, -0.4) * mm});
            skLineSegment(sketch, "E83.top", {"start": v(45.88, -0.93) * mm, "end": v(44.83, 0.12) * mm});
            skLineSegment(sketch, "E83.right", {"start": v(45.88, 1.16) * mm, "end": v(44.83, 0.12) * mm});
            skSolve(sketch);
        }
        {
            var Q0;
            Q0 = qSketchRegion(id + "F38", true);
            extrude(context, id + "F39", {"entities" : qUnion([Q0]), "operationType" : NewBodyOperationType.REMOVE, "oppositeDirection" : true, "depth" : 2 * mm, "offsetDistance" : 25 * mm});
        }
        {
            var Q0;
            Q0=qCreatedBy(makeId("Front.planeOp"),FACE);
            cPlane(context, id + "F40", {"entities" : qUnion([Q0]), "cplaneType" : CPlaneType.OFFSET, "offset" : 40 * mm, "oppositeDirection" : true, "width" : 150 * mm, "height" : 150 * mm});
        }
        {
            var Q0;
            Q0=qCreatedBy(id+"F40.planeOp",FACE);
            var sketch = newSketch(context, id + "F41", { "sketchPlane" : qUnion([Q0])});
            skCircle(sketch, "E84", {"center": v(0, -24.51) * mm, "radius": 1.75 * mm});
            skSolve(sketch);
        }
        {
            var Q0;
            Q0=makeQuery(id+"F41.imprint","IMPRINT",FACE,{"disambiguationData":[TD([[makeQuery(id+"F41.imprint","IMPRINT",EDGE,{"derivedFrom":sQuery(id+"F41.wireOp",EDGE,"E84")}),1.0]])]});
            extrude(context, id + "F42", {"entities" : qUnion([Q0]), "operationType" : NewBodyOperationType.REMOVE, "depth" : 20 * mm, "offsetDistance" : 25 * mm});
        }
        {
            var Q0;
            Q0=makeQuery(id+"F1.opExtrude","SWEPT_FACE",FACE,{"disambiguationData":[OSD([sQuery(id+"F0.wireOp",EDGE,"E0.bottom")])]});
            var sketch = newSketch(context, id + "F43", { "sketchPlane" : qUnion([Q0])});
            skLineSegment(sketch, "E85.bottom", {"start": v(-1.43, 26.17) * mm, "end": v(-1.81, 26.17) * mm});
            skLineSegment(sketch, "E85.top", {"start": v(-1.43, 16.17) * mm, "end": v(-1.81, 16.17) * mm});
            skLineSegment(sketch, "E85.left", {"start": v(2.19, 24) * mm, "end": v(2.19, 18.34) * mm});
            skLineSegment(sketch, "E85.right", {"start": v(-2.81, 25.17) * mm, "end": v(-2.81, 17.17) * mm});
            skPoint(sketch, "E85.middle", {"position": v(-0.31, 21.17) * mm});
            skPoint(sketch, "E86", {"position": v(-1.22, 16.17) * mm});
            skPoint(sketch, "E87", {"position": v(-1.22, 26.17) * mm});
            skLineSegment(sketch, "E88", {"start": v(-1.03, 16.26) * mm, "end": v(1.6, 17.42) * mm});
            skLineSegment(sketch, "E89.MirrorCS", {"start": v(-1.03, 26.09) * mm, "end": v(1.6, 24.92) * mm});
            skPoint(sketch, "E90.visualSharp", {"position": v(-2.81, 16.17) * mm});
            skArc(sketch, "E90.filletArc", {"start": v(-2.81, 17.17) * mm, "mid": v(-2.52, 16.47) * mm, "end": v(-1.81, 16.17) * mm});
            skPoint(sketch, "E91.visualSharp", {"position": v(-2.81, 26.17) * mm});
            skArc(sketch, "E91.filletArc", {"start": v(-1.81, 26.17) * mm, "mid": v(-2.52, 25.88) * mm, "end": v(-2.81, 25.17) * mm});
            skPoint(sketch, "E92.orphan", {"position": v(2.19, 16.17) * mm});
            skPoint(sketch, "E93.orphan", {"position": v(2.19, 26.17) * mm});
            skPoint(sketch, "E94.visualSharp", {"position": v(2.19, 17.69) * mm});
            skArc(sketch, "E94.filletArc", {"start": v(1.6, 17.42) * mm, "mid": v(2.03, 17.8) * mm, "end": v(2.19, 18.34) * mm});
            skPoint(sketch, "E95.visualSharp", {"position": v(2.19, 24.66) * mm});
            skArc(sketch, "E95.filletArc", {"start": v(2.19, 24) * mm, "mid": v(2.03, 24.55) * mm, "end": v(1.6, 24.92) * mm});
            skArc(sketch, "E96.filletArc", {"start": v(-1.03, 26.09) * mm, "mid": v(-1.23, 26.15) * mm, "end": v(-1.43, 26.17) * mm});
            skArc(sketch, "E97.filletArc", {"start": v(-1.43, 16.17) * mm, "mid": v(-1.23, 16.2) * mm, "end": v(-1.03, 16.26) * mm});
            skSolve(sketch);
        }
        {
            var Q0;
            Q0=makeQuery(id+"F43.imprint","IMPRINT",FACE,{"disambiguationData":[TD([[makeQuery(id+"F43.imprint","IMPRINT",EDGE,{"derivedFrom":sQuery(id+"F43.wireOp",EDGE,"E85.bottom")}),1.0]])]});
            extrude(context, id + "F44", {"entities" : qUnion([Q0]), "operationType" : NewBodyOperationType.REMOVE, "oppositeDirection" : true, "depth" : 10 * mm, "offsetDistance" : 25 * mm});
        }
    });
